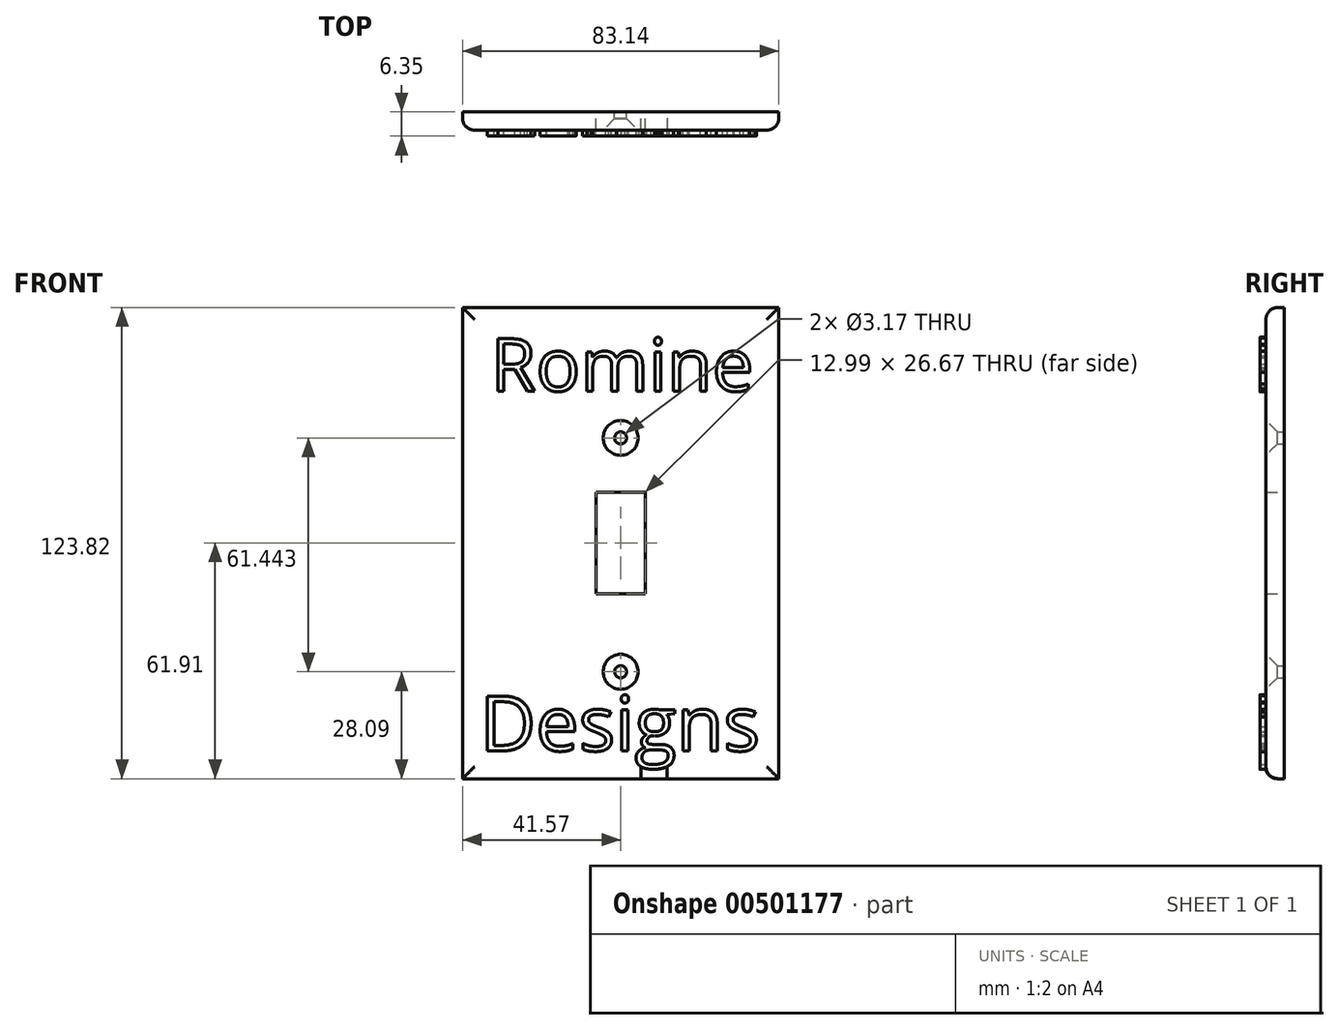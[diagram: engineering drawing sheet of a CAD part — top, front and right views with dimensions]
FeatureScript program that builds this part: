
annotation { "Feature Type Name" : "Feature", "Feature Type Description" : "" }
export const myFeature = defineFeature(function(context is Context, id is Id, definition is map)
    precondition{}
    {
        {
            var Q0;
            Q0=qCreatedBy(makeId("Front.planeOp"),FACE);
            var sketch = newSketch(context, id + "F0", { "sketchPlane" : qUnion([Q0])});
            skLineSegment(sketch, "E0.bottom", {"start": v(-41.57, 61.91) * mm, "end": v(41.57, 61.91) * mm});
            skLineSegment(sketch, "E0.top", {"start": v(-41.57, -61.91) * mm, "end": v(41.57, -61.91) * mm});
            skLineSegment(sketch, "E0.left", {"start": v(-41.57, 61.91) * mm, "end": v(-41.57, -61.91) * mm});
            skLineSegment(sketch, "E0.right", {"start": v(41.57, 61.91) * mm, "end": v(41.57, -61.91) * mm});
            skLineSegment(sketch, "E1.bottom", {"start": v(-6.5, 13.33) * mm, "end": v(6.5, 13.33) * mm});
            skLineSegment(sketch, "E1.top", {"start": v(-6.5, -13.33) * mm, "end": v(6.5, -13.33) * mm});
            skLineSegment(sketch, "E1.left", {"start": v(-6.5, 13.33) * mm, "end": v(-6.5, -13.33) * mm});
            skLineSegment(sketch, "E1.right", {"start": v(6.5, 13.33) * mm, "end": v(6.5, -13.33) * mm});
            skCircle(sketch, "E2", {"center": v(0, -33.82) * mm, "radius": 1.59 * mm});
            skCircle(sketch, "E3", {"center": v(0, 27.62) * mm, "radius": 1.59 * mm});
            skSolve(sketch);
        }
        {
            var Q0;
            Q0=makeQuery(id+"F0.imprint","IMPRINT",FACE,{"disambiguationData":[TD([[makeQuery(id+"F0.imprint","IMPRINT",EDGE,{"derivedFrom":sQuery(id+"F0.wireOp",EDGE,"E0.bottom")}),-1.0]])]});
            extrude(context, id + "F1", {"entities" : qUnion([Q0]), "depth" : 4.76 * mm, "offsetDistance" : 25.4 * mm});
        }
        {
            var Q0;
            Q0=makeQuery(id+"F1.opExtrude","CAP_EDGE",EDGE,{"disambiguationData":[OSD([sQuery(id+"F0.wireOp",EDGE,"E3")])],"isStart":false});
            var Q1;
            Q1=makeQuery(id+"F1.opExtrude","CAP_EDGE",EDGE,{"disambiguationData":[OSD([sQuery(id+"F0.wireOp",EDGE,"E2")])],"isStart":false});
            chamfer(context, id + "F2", {"entities" : qUnion([Q0, Q1]), "width" : 3 * mm, "tangentPropagation" : true});
        }
        {
            var Q0;
            Q0=makeQuery(id+"F1.opExtrude","CAP_FACE",FACE,{"disambiguationData":[OSD([sQuery(id+"F0.wireOp",EDGE,"E0.bottom"),sQuery(id+"F0.wireOp",EDGE,"E0.top"),sQuery(id+"F0.wireOp",EDGE,"E0.left"),sQuery(id+"F0.wireOp",EDGE,"E0.right"),sQuery(id+"F0.wireOp",EDGE,"E1.bottom"),sQuery(id+"F0.wireOp",EDGE,"E1.top"),sQuery(id+"F0.wireOp",EDGE,"E1.left"),sQuery(id+"F0.wireOp",EDGE,"E1.right"),sQuery(id+"F0.wireOp",EDGE,"E2"),sQuery(id+"F0.wireOp",EDGE,"E3")])],"isStart":false});
            var sketch = newSketch(context, id + "F3", { "sketchPlane" : qUnion([Q0])});
            skText(sketch, "E4", { "text": "Romine", "fontName": "OpenSans-Regular.ttf"});
            skText(sketch, "E5", { "text": "Designs", "fontName": "OpenSans-Regular.ttf"});
            const initialGuessF3  = {"E4": [-0.03419, 0.0399, 1, 0, 0.0139], "E5": [-0.03695, -0.0546, 1, 0, 0.01447]};
            skSetInitialGuess(sketch, initialGuessF3);
            skSolve(sketch);
        }
        {
            var Q0;
            Q0 = qSketchRegion(id + "F3", true);
            extrude(context, id + "F4", {"entities" : qUnion([Q0]), "operationType" : NewBodyOperationType.ADD, "depth" : 1.59 * mm});
        }
        {
            var Q0;
            Q0=makeQuery(id+"F1.opExtrude","CAP_EDGE",EDGE,{"disambiguationData":[OSD([sQuery(id+"F0.wireOp",EDGE,"E0.left")])],"isStart":false});
            var Q1;
            Q1=makeQuery(id+"F1.opExtrude","CAP_EDGE",EDGE,{"disambiguationData":[OSD([sQuery(id+"F0.wireOp",EDGE,"E0.right")])],"isStart":false});
            var Q2;
            Q2=makeQuery(id+"F1.opExtrude","CAP_EDGE",EDGE,{"disambiguationData":[OSD([sQuery(id+"F0.wireOp",EDGE,"E0.bottom")])],"isStart":false});
            var Q3;
            Q3=makeQuery(id+"F1.opExtrude","CAP_EDGE",EDGE,{"disambiguationData":[OSD([sQuery(id+"F0.wireOp",EDGE,"E0.top")])],"isStart":false});
            fillet(context, id + "F5", {"entities" : qUnion([Q0, Q1, Q2, Q3]), "radius" : 3.17 * mm, "tangentPropagation" : true, "allowEdgeOverflow" : false});
        }
    });
